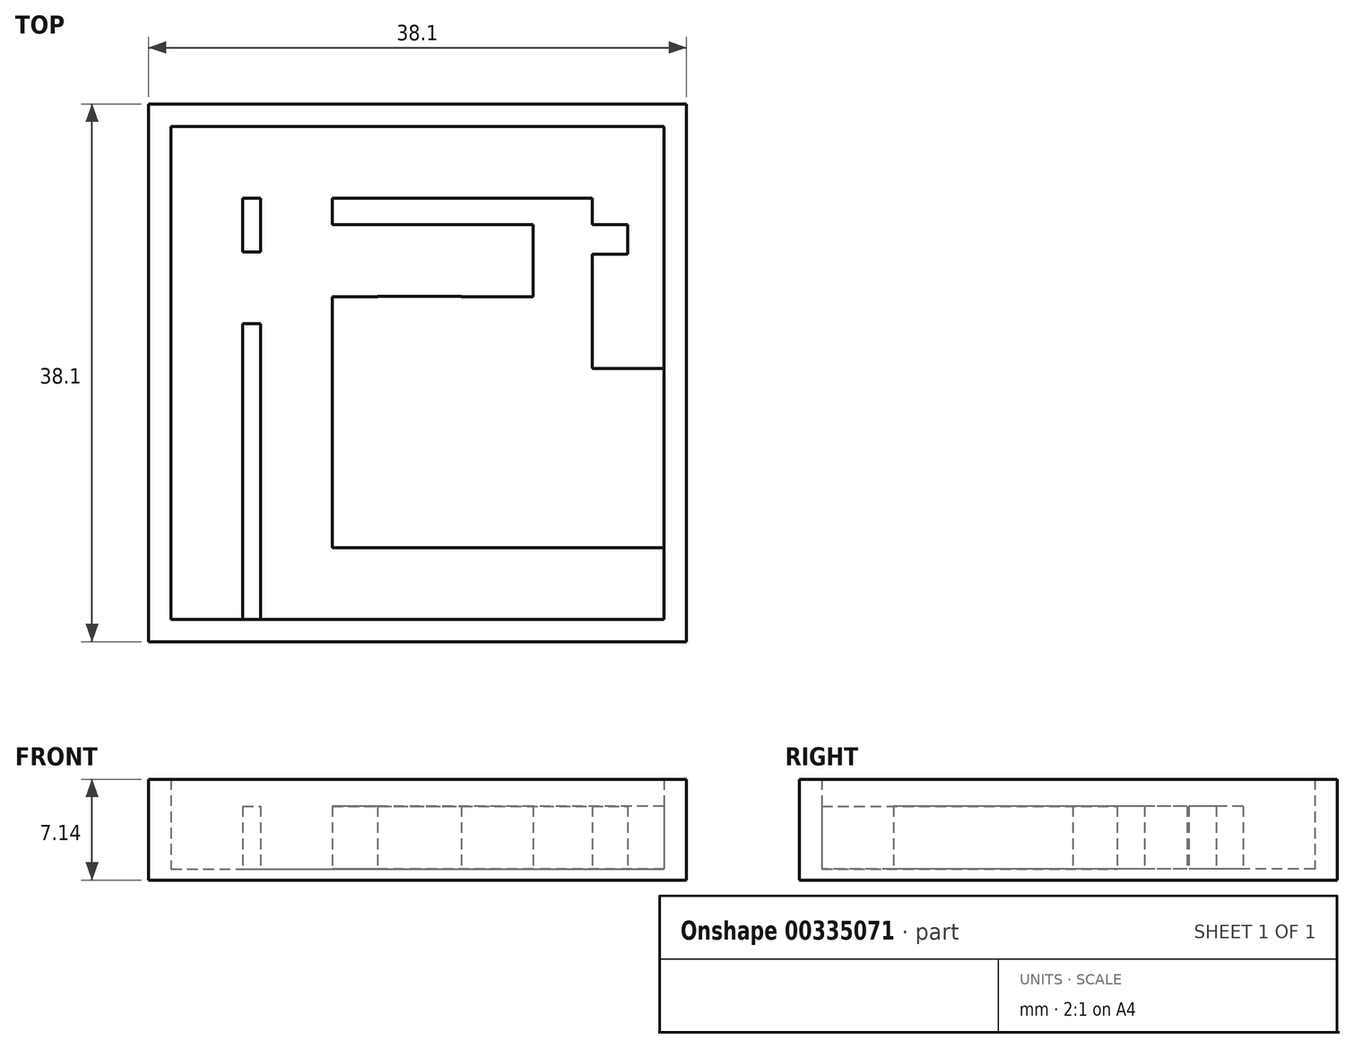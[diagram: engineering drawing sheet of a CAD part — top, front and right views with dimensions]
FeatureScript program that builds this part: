
annotation { "Feature Type Name" : "Feature", "Feature Type Description" : "" }
export const myFeature = defineFeature(function(context is Context, id is Id, definition is map)
    precondition{}
    {
        {
            var Q0;
            Q0=qCreatedBy(makeId("Top.planeOp"),FACE);
            var sketch = newSketch(context, id + "F0", { "sketchPlane" : qUnion([Q0])});
            skLineSegment(sketch, "E0.bottom", {"start": v(-24.44, 25.03) * mm, "end": v(13.66, 25.03) * mm});
            skLineSegment(sketch, "E0.top", {"start": v(-24.44, -13.07) * mm, "end": v(13.66, -13.07) * mm});
            skLineSegment(sketch, "E0.left", {"start": v(-24.44, 25.03) * mm, "end": v(-24.44, -13.07) * mm});
            skLineSegment(sketch, "E0.right", {"start": v(13.66, 25.03) * mm, "end": v(13.66, -13.07) * mm});
            skSolve(sketch);
        }
        {
            var Q0;
            Q0=makeQuery(id+"F0.imprint","IMPRINT",FACE,{"disambiguationData":[TD([[makeQuery(id+"F0.imprint","IMPRINT",EDGE,{"derivedFrom":sQuery(id+"F0.wireOp",EDGE,"E0.bottom")}),-1.0]])]});
            extrude(context, id + "F1", {"entities" : qUnion([Q0]), "depth" : 0.8 * mm});
        }
        {
            var Q0;
            Q0=makeQuery(id+"F1.opExtrude","CAP_FACE",FACE,{"disambiguationData":[OSD([sQuery(id+"F0.wireOp",EDGE,"E0.bottom"),sQuery(id+"F0.wireOp",EDGE,"E0.top"),sQuery(id+"F0.wireOp",EDGE,"E0.left"),sQuery(id+"F0.wireOp",EDGE,"E0.right")])],"isStart":false});
            var sketch = newSketch(context, id + "F2", { "sketchPlane" : qUnion([Q0])});
            skLineSegment(sketch, "E1.0", {"start": v(-22.85, 23.44) * mm, "end": v(12.07, 23.44) * mm});
            skLineSegment(sketch, "E1.1", {"start": v(-22.85, 23.44) * mm, "end": v(-22.85, -11.48) * mm});
            skLineSegment(sketch, "E1.2", {"start": v(-22.85, -11.48) * mm, "end": v(12.07, -11.48) * mm});
            skLineSegment(sketch, "E1.3", {"start": v(12.07, 23.44) * mm, "end": v(12.07, -11.48) * mm});
            skSolve(sketch);
        }
        {
            var Q0;
            Q0=makeQuery(id+"F2.imprint","IMPRINT",FACE,{"disambiguationData":[TD([[makeQuery(id+"F2.imprint","IMPRINT",EDGE,{"derivedFrom":sQuery(id+"F2.wireOp",EDGE,"E1.0")}),1.0]])]});
            extrude(context, id + "F3", {"entities" : qUnion([Q0]), "operationType" : NewBodyOperationType.ADD, "depth" : 6.35 * mm});
        }
        {
            var Q0;
            Q0=makeQuery(id+"F1.opExtrude","CAP_FACE",FACE,{"disambiguationData":[OSD([sQuery(id+"F0.wireOp",EDGE,"E0.bottom"),sQuery(id+"F0.wireOp",EDGE,"E0.top"),sQuery(id+"F0.wireOp",EDGE,"E0.left"),sQuery(id+"F0.wireOp",EDGE,"E0.right")])],"isStart":false});
            var sketch = newSketch(context, id + "F4", { "sketchPlane" : qUnion([Q0])});
            skLineSegment(sketch, "E2.bottom", {"start": v(-17, -11.48) * mm, "end": v(-17.77, -11.48) * mm});
            skLineSegment(sketch, "E2.top", {"start": v(-17, 18.36) * mm, "end": v(-17.77, 18.36) * mm});
            skLineSegment(sketch, "E3", {"start": v(-22.85, -11.48) * mm, "end": v(-17.77, -11.48) * mm});
            skLineSegment(sketch, "E4", {"start": v(-17.77, 18.36) * mm, "end": v(-17, 18.36) * mm});
            skLineSegment(sketch, "E5.bottom", {"start": v(-17.77, -11.48) * mm, "end": v(-16.5, -11.48) * mm});
            skLineSegment(sketch, "E5.top", {"start": v(-17.77, 17.85) * mm, "end": v(-16.5, 17.85) * mm});
            skLineSegment(sketch, "E5.left", {"start": v(-17.77, 16.64) * mm, "end": v(-17.77, 17.85) * mm});
            skLineSegment(sketch, "E6.left", {"start": v(-17.77, 18.36) * mm, "end": v(-17.77, 16.64) * mm});
            skLineSegment(sketch, "E7.bottom", {"start": v(-11.42, 18.36) * mm, "end": v(2.8, 18.36) * mm});
            skLineSegment(sketch, "E7.top", {"start": v(-11.42, 16.46) * mm, "end": v(2.8, 16.46) * mm});
            skLineSegment(sketch, "E7.left", {"start": v(-11.42, 18.36) * mm, "end": v(-11.42, 16.46) * mm});
            skLineSegment(sketch, "E7.right", {"start": v(2.8, 18.36) * mm, "end": v(2.8, 16.46) * mm});
            skLineSegment(sketch, "E8.bottom", {"start": v(2.8, 18.36) * mm, "end": v(7, 18.36) * mm});
            skLineSegment(sketch, "E8.top", {"start": v(2.8, 11.38) * mm, "end": v(7, 11.38) * mm});
            skLineSegment(sketch, "E8.left", {"start": v(2.8, 18.36) * mm, "end": v(2.8, 11.38) * mm});
            skLineSegment(sketch, "E8.right", {"start": v(7, 18.36) * mm, "end": v(7, 11.38) * mm});
            skLineSegment(sketch, "E9.bottom", {"start": v(7, 11.38) * mm, "end": v(-11.42, 11.38) * mm});
            skLineSegment(sketch, "E9.top", {"start": v(7, 3.96) * mm, "end": v(-11.42, 3.96) * mm});
            skLineSegment(sketch, "E9.left", {"start": v(7, 3.96) * mm, "end": v(7, 11.38) * mm});
            skLineSegment(sketch, "E9.right", {"start": v(-11.42, 3.96) * mm, "end": v(-11.42, 11.38) * mm});
            skLineSegment(sketch, "E10.bottom", {"start": v(-8.23, 11.38) * mm, "end": v(-2.28, 11.38) * mm});
            skLineSegment(sketch, "E10.top", {"start": v(-8.23, 11.38) * mm, "end": v(-2.28, 11.38) * mm});
            skLineSegment(sketch, "E10.left", {"start": v(-8.23, 11.38) * mm, "end": v(-8.23, 11.38) * mm});
            skLineSegment(sketch, "E10.right", {"start": v(-2.28, 11.38) * mm, "end": v(-2.28, 11.38) * mm});
            skLineSegment(sketch, "E11.bottom", {"start": v(7, 16.46) * mm, "end": v(9.5, 16.46) * mm});
            skLineSegment(sketch, "E11.top", {"start": v(7, 14.4) * mm, "end": v(9.5, 14.4) * mm});
            skLineSegment(sketch, "E11.left", {"start": v(7, 16.46) * mm, "end": v(7, 14.4) * mm});
            skLineSegment(sketch, "E11.right", {"start": v(9.5, 16.46) * mm, "end": v(9.5, 14.4) * mm});
            skLineSegment(sketch, "E12.bottom", {"start": v(12.07, 6.3) * mm, "end": v(-11.42, 6.3) * mm});
            skLineSegment(sketch, "E12.top", {"start": v(12.07, -6.4) * mm, "end": v(-11.42, -6.4) * mm});
            skLineSegment(sketch, "E12.left", {"start": v(12.07, 6.3) * mm, "end": v(12.07, -6.4) * mm});
            skLineSegment(sketch, "E12.right", {"start": v(-11.42, 6.3) * mm, "end": v(-11.42, -6.4) * mm});
            skLineSegment(sketch, "E13.bottom", {"start": v(-17.77, -11.48) * mm, "end": v(-12.7, -11.48) * mm});
            skLineSegment(sketch, "E14.bottom", {"start": v(-17.77, 18.36) * mm, "end": v(-16.5, 18.36) * mm});
            skLineSegment(sketch, "E14.top", {"start": v(-17.77, 14.53) * mm, "end": v(-16.5, 14.53) * mm});
            skLineSegment(sketch, "E14.left", {"start": v(-17.77, 18.36) * mm, "end": v(-17.77, 14.53) * mm});
            skLineSegment(sketch, "E14.right", {"start": v(-16.5, 18.36) * mm, "end": v(-16.5, 14.53) * mm});
            skLineSegment(sketch, "E15.top", {"start": v(-17.77, 9.45) * mm, "end": v(-16.5, 9.45) * mm});
            skLineSegment(sketch, "E15.left", {"start": v(-17.77, -11.48) * mm, "end": v(-17.77, 9.45) * mm});
            skLineSegment(sketch, "E15.right", {"start": v(-16.5, -11.48) * mm, "end": v(-16.5, 9.45) * mm});
            skSolve(sketch);
        }
        {
            var Q0;
            Q0=qSketchRegion(id+"F4",true);
            extrude(context, id + "F5", {"entities" : qUnion([Q0]), "operationType" : NewBodyOperationType.ADD, "depth" : 4.44 * mm});
        }
    });
